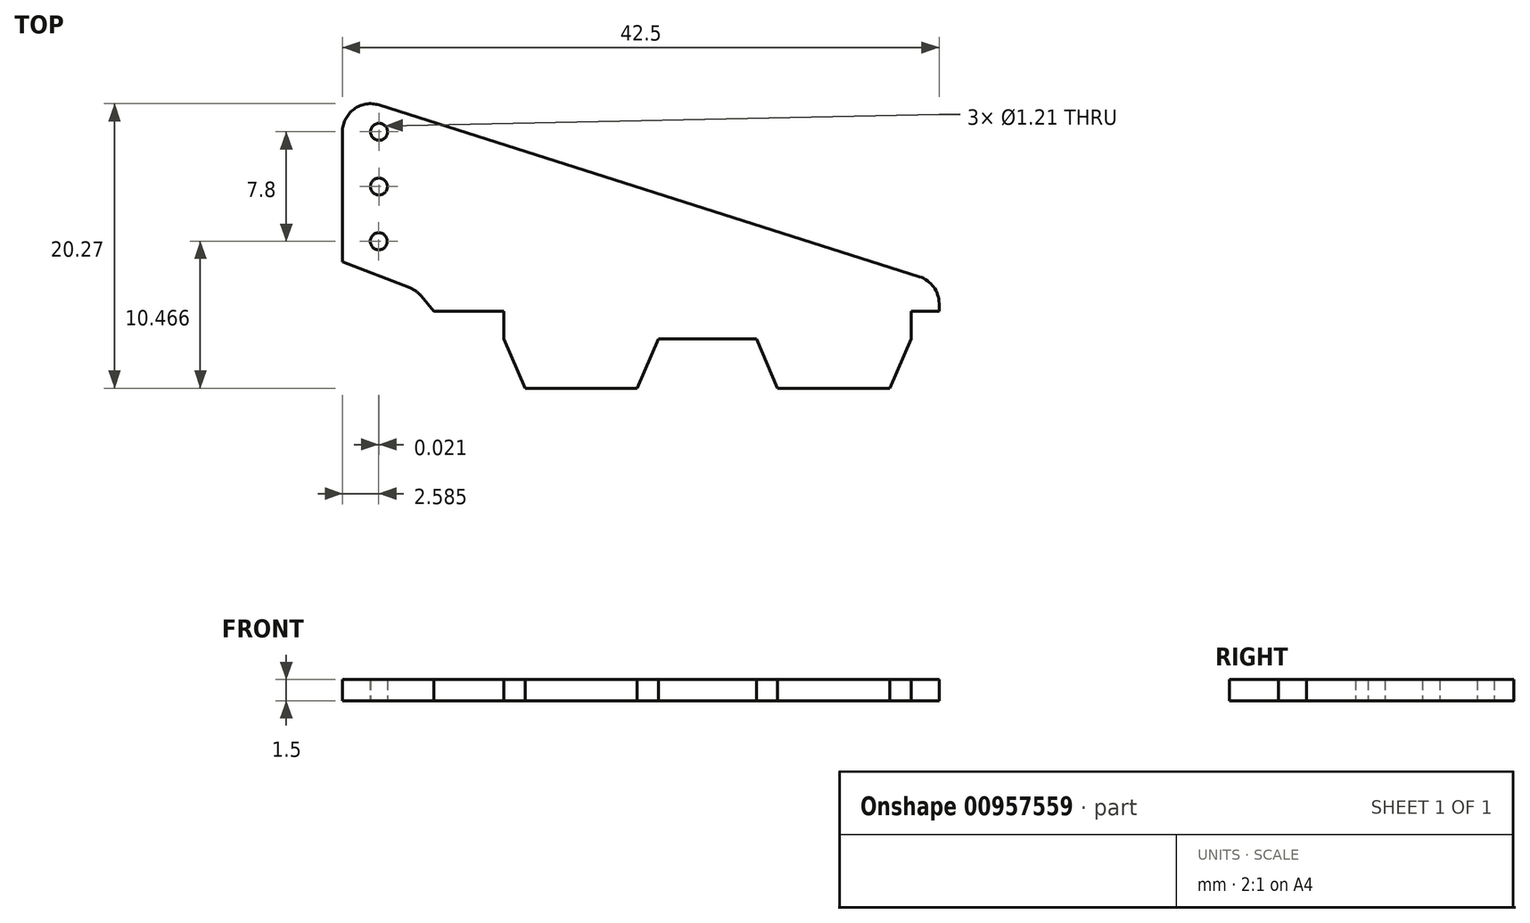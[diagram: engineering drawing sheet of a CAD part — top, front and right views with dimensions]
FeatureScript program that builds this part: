
annotation { "Feature Type Name" : "Feature", "Feature Type Description" : "" }
export const myFeature = defineFeature(function(context is Context, id is Id, definition is map)
    precondition{}
    {
        {
            var Q0;
            Q0=qCreatedBy(makeId("Top.planeOp"),FACE);
            var sketch = newSketch(context, id + "F0", { "sketchPlane" : qUnion([Q0])});
            skLineSegment(sketch, "E0", {"start": v(0, 0) * mm, "end": v(-8, 0) * mm});
            skLineSegment(sketch, "E1", {"start": v(-9.5, 3.5) * mm, "end": v(-8, 0) * mm});
            skLineSegment(sketch, "E2", {"start": v(-9.5, 3.5) * mm, "end": v(-16.5, 3.5) * mm});
            skLineSegment(sketch, "E3", {"start": v(-18, 0) * mm, "end": v(-16.5, 3.5) * mm});
            skLineSegment(sketch, "E4", {"start": v(-18, 0) * mm, "end": v(-26, 0) * mm});
            skLineSegment(sketch, "E5", {"start": v(-27.5, 3.5) * mm, "end": v(-26, 0) * mm});
            skLineSegment(sketch, "E6", {"start": v(-27.5, 3.5) * mm, "end": v(-27.5, 5.5) * mm});
            skLineSegment(sketch, "E7", {"start": v(-27.5, 5.5) * mm, "end": v(-32.5, 5.5) * mm});
            skLineSegment(sketch, "E8", {"start": v(1.5, 3.5) * mm, "end": v(0, 0) * mm});
            skLineSegment(sketch, "E9", {"start": v(1.5, 3.5) * mm, "end": v(1.5, 5.5) * mm});
            skLineSegment(sketch, "E10", {"start": v(1.5, 5.5) * mm, "end": v(3.5, 5.5) * mm});
            skLineSegment(sketch, "E11", {"start": v(3.5, 5.5) * mm, "end": v(3.5, 6.04) * mm});
            skLineSegment(sketch, "E12", {"start": v(-26, 0) * mm, "end": v(-39, 0) * mm});
            skLineSegment(sketch, "E13", {"start": v(-36.4, 20.17) * mm, "end": v(2.1, 7.94) * mm});
            skLineSegment(sketch, "E14", {"start": v(-39, 18.27) * mm, "end": v(-39, 9) * mm});
            skLineSegment(sketch, "E15", {"start": v(-39, 9) * mm, "end": v(-34.2, 7.15) * mm});
            skLineSegment(sketch, "E16", {"start": v(-33.38, 6.56) * mm, "end": v(-32.5, 5.5) * mm});
            skPoint(sketch, "E17.visualSharp", {"position": v(-39, 21) * mm});
            skArc(sketch, "E17.filletArc", {"start": v(-36.4, 20.17) * mm, "mid": v(-38.18, 19.88) * mm, "end": v(-39, 18.27) * mm});
            skPoint(sketch, "E18.visualSharp", {"position": v(3.5, 7.5) * mm});
            skArc(sketch, "E18.filletArc", {"start": v(3.5, 6.04) * mm, "mid": v(3.11, 7.22) * mm, "end": v(2.1, 7.94) * mm});
            skPoint(sketch, "E19.visualSharp", {"position": v(-33.71, 6.96) * mm});
            skArc(sketch, "E19.filletArc", {"start": v(-33.38, 6.56) * mm, "mid": v(-33.75, 6.91) * mm, "end": v(-34.2, 7.15) * mm});
            skCircle(sketch, "E20", {"center": v(-36.4, 18.27) * mm, "radius": 0.6 * mm});
            skCircle(sketch, "E21.1.0.0", {"center": v(-36.4, 14.37) * mm, "radius": 0.6 * mm});
            skCircle(sketch, "E21.2.0.0", {"center": v(-36.42, 10.47) * mm, "radius": 0.6 * mm});
            skLineSegment(sketch, "E21.direction1", {"start": v(-36.4, 18.27) * mm, "end": v(-36.4, 14.37) * mm, "construction": true});
            skSolve(sketch);
        }
        {
            var Q0;
            Q0=makeQuery(id+"F0.imprint","IMPRINT",FACE,{"disambiguationData":[TD([[makeQuery(id+"F0.imprint","IMPRINT",EDGE,{"derivedFrom":sQuery(id+"F0.wireOp",EDGE,"E0")}),-1.0]])]});
            extrude(context, id + "F1", {"entities" : qUnion([Q0]), "depth" : 1.5 * mm, "offsetDistance" : 25 * mm});
        }
    });
